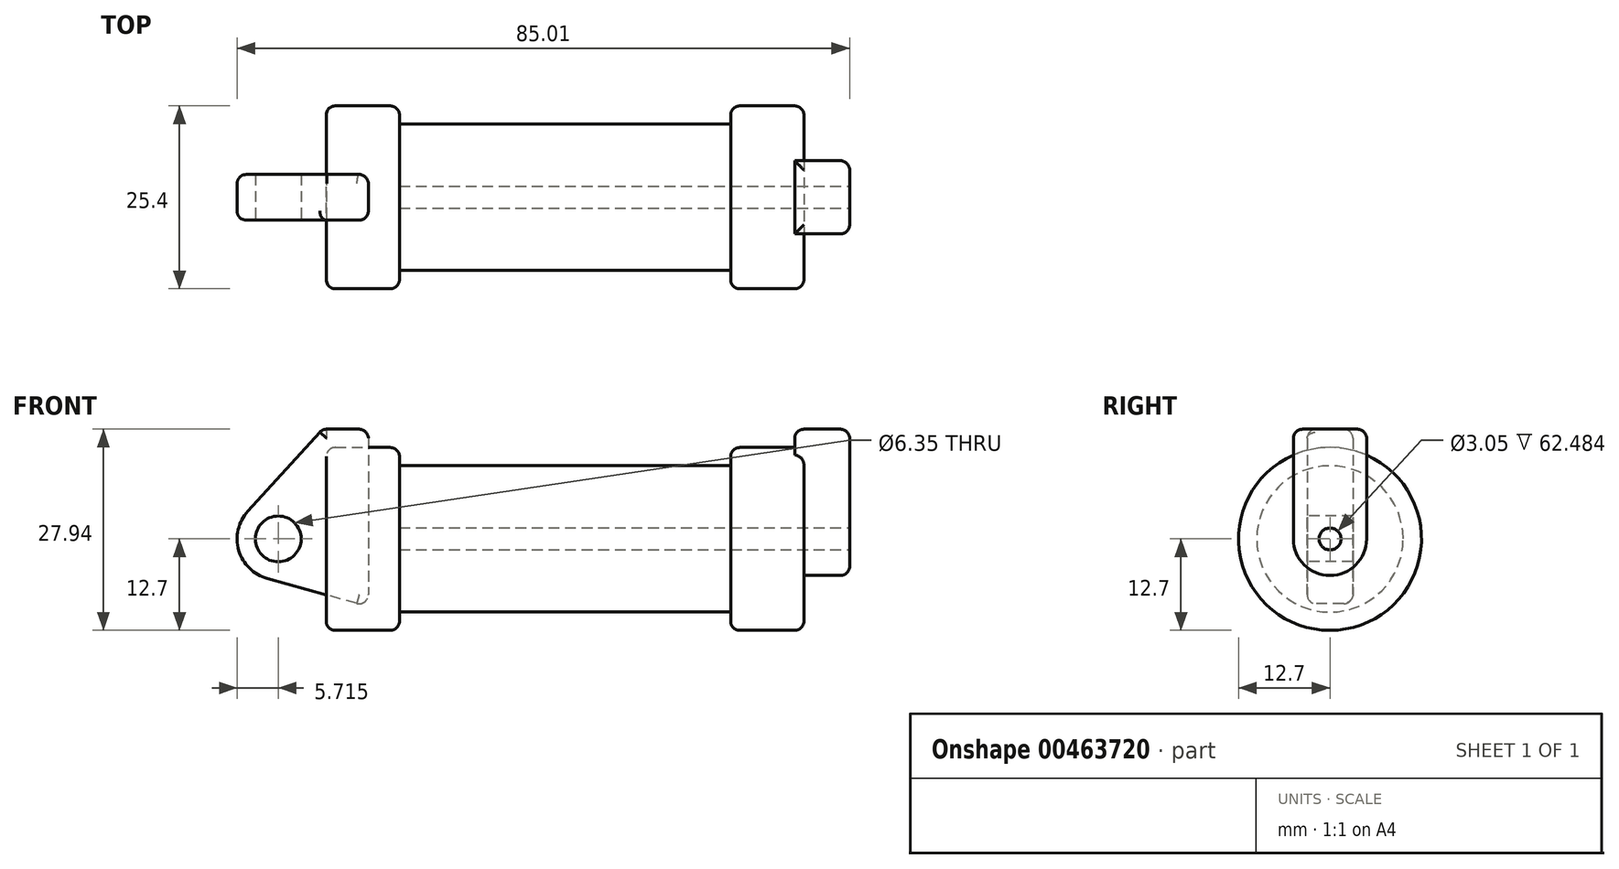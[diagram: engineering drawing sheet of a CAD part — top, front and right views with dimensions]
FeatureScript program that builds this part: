
annotation { "Feature Type Name" : "Feature", "Feature Type Description" : "" }
export const myFeature = defineFeature(function(context is Context, id is Id, definition is map)
    precondition{}
    {
        {
            var Q0;
            Q0=qCreatedBy(makeId("Front.planeOp"),FACE);
            var sketch = newSketch(context, id + "F0", { "sketchPlane" : qUnion([Q0])});
            skLineSegment(sketch, "E0", {"start": v(0, 0) * mm, "end": v(0, 12.7) * mm});
            skLineSegment(sketch, "E1", {"start": v(0, 12.7) * mm, "end": v(10.16, 12.7) * mm});
            skLineSegment(sketch, "E2", {"start": v(10.16, 12.7) * mm, "end": v(10.16, 10.16) * mm});
            skLineSegment(sketch, "E3", {"start": v(10.16, 10.16) * mm, "end": v(56.13, 10.16) * mm});
            skLineSegment(sketch, "E4", {"start": v(56.13, 10.16) * mm, "end": v(56.13, 12.7) * mm});
            skLineSegment(sketch, "E5", {"start": v(56.13, 12.7) * mm, "end": v(66.3, 12.7) * mm});
            skLineSegment(sketch, "E6", {"start": v(66.3, 12.7) * mm, "end": v(66.3, 0) * mm});
            skLineSegment(sketch, "E7", {"start": v(66.3, 0) * mm, "end": v(0, 0) * mm});
            skLineSegment(sketch, "E8", {"start": v(5.84, 15.24) * mm, "end": v(-0.5, 15.24) * mm});
            skLineSegment(sketch, "E9", {"start": v(-0.5, 15.24) * mm, "end": v(-10.88, 3.85) * mm});
            skLineSegment(sketch, "E10", {"start": v(0, 0) * mm, "end": v(-6.65, 0) * mm});
            skCircle(sketch, "E11", {"center": v(-6.65, 0) * mm, "radius": 5.72 * mm});
            skCircle(sketch, "E12", {"center": v(-6.65, 0) * mm, "radius": 3.18 * mm});
            skLineSegment(sketch, "E13", {"start": v(5.84, 15.24) * mm, "end": v(5.84, -9.4) * mm});
            skLineSegment(sketch, "E14", {"start": v(5.84, -9.4) * mm, "end": v(-8.18, -5.5) * mm});
            skSolve(sketch);
        }
        {
            var Q0;
            {var subQ0=sQuery(id+"F0.wireOp",EDGE,"E0");Q0=makeQuery(id+"F0.imprint","IMPRINT",FACE,{"disambiguationData":[TD([[makeQuery(id+"F0.imprint","IMPRINT",EDGE,{"derivedFrom":subQ0}),-1.0]])]});}
            var Q1;
            {var subQ1=sQuery(id+"F0.wireOp",EDGE,"E0");Q1=makeQuery(id+"F0.imprint","IMPRINT",FACE,{"disambiguationData":[TD([[makeQuery(id+"F0.imprint","IMPRINT",EDGE,{"derivedFrom":subQ1}),1.0]])]});}
            var Q2;
            {var subQ0=sQuery(id+"F0.wireOp",EDGE,"E14");Q2=makeQuery(id+"F0.imprint","IMPRINT",FACE,{"disambiguationData":[TD([[makeQuery(id+"F0.imprint","IMPRINT",EDGE,{"derivedFrom":subQ0}),-1.0]])]});}
            var Q3;
            {var subQ5=sQuery(id+"F0.wireOp",EDGE,"E12");Q3=makeQuery(id+"F0.imprint","IMPRINT",FACE,{"disambiguationData":[TD([[makeQuery(id+"F0.imprint","IMPRINT",EDGE,{"derivedFrom":subQ5}),-1.0]])]});}
            extrude(context, id + "F1", {"entities" : qUnion([Q0, Q1, Q2, Q3]), "endBound" : BoundingType.SYMMETRIC, "oppositeDirection" : true, "depth" : 6.35 * mm});
        }
        {
            var Q0;
            {var subQ0=sQuery(id+"F0.wireOp",EDGE,"E2");Q0=makeQuery(id+"F0.imprint","IMPRINT",FACE,{"disambiguationData":[TD([[makeQuery(id+"F0.imprint","IMPRINT",EDGE,{"derivedFrom":subQ0}),-1.0]])]});}
            var Q1;
            {var subQ0=sQuery(id+"F0.wireOp",EDGE,"E0");Q1=makeQuery(id+"F0.imprint","IMPRINT",FACE,{"disambiguationData":[TD([[makeQuery(id+"F0.imprint","IMPRINT",EDGE,{"derivedFrom":subQ0}),-1.0]])]});}
            var Q2;
            Q2=sQuery(id+"F0.wireOp",EDGE,"E7");
            revolve(context, id + "F2", {"entities" : qUnion([Q0, Q1]), "axis" : qUnion([Q2]), "revolveType" : RevolveType.FULL});
        }
        {
            var Q0;
            Q0=makeQuery(id+"F2.opRevolve","SWEPT_FACE",FACE,{"disambiguationData":[OSD([sQuery(id+"F0.wireOp",EDGE,"E6")])]});
            var sketch = newSketch(context, id + "F3", { "sketchPlane" : qUnion([Q0])});
            skCircle(sketch, "E15", {"center": v(0, 0) * mm, "radius": 1.52 * mm});
            skCircle(sketch, "E16", {"center": v(0, 0) * mm, "radius": 5.08 * mm});
            skLineSegment(sketch, "E17", {"start": v(5.08, 0) * mm, "end": v(5.08, 15.24) * mm});
            skLineSegment(sketch, "E18", {"start": v(-5.08, 0) * mm, "end": v(-5.08, 15.24) * mm});
            skLineSegment(sketch, "E19", {"start": v(-5.08, 15.24) * mm, "end": v(5.08, 15.24) * mm});
            skSolve(sketch);
        }
        {
            var Q0;
            Q0=makeQuery(id+"F3.imprint","IMPRINT",FACE,{"disambiguationData":[TD([[makeQuery(id+"F3.imprint","IMPRINT",EDGE,{"derivedFrom":sQuery(id+"F3.wireOp",EDGE,"E15")}),1.0]])]});
            var Q1;
            Q1=makeQuery(id+"F2.opRevolve","SWEPT_FACE",FACE,{"disambiguationData":[OSD([sQuery(id+"F0.wireOp",EDGE,"E2")])]});
            extrude(context, id + "F4", {"entities" : qUnion([Q0]), "operationType" : NewBodyOperationType.REMOVE, "endBound" : BoundingType.UP_TO_SURFACE, "oppositeDirection" : true, "endBoundEntityFace" : qUnion([Q1]), "depth" : 25.4 * mm});
        }
        {
            var Q0;
            {var subQ0=sQuery(id+"F3.wireOp",EDGE,"E19");Q0=makeQuery(id+"F3.imprint","IMPRINT",FACE,{"disambiguationData":[TD([[makeQuery(id+"F3.imprint","IMPRINT",EDGE,{"derivedFrom":subQ0}),-1.0]])]});}
            extrude(context, id + "F5", {"entities" : qUnion([Q0]), "operationType" : NewBodyOperationType.ADD, "oppositeDirection" : true, "depth" : 1.27 * mm});
        }
        {
            var Q0;
            Q0 = qSketchRegion(id + "F3", true);
            extrude(context, id + "F6", {"entities" : qUnion([Q0]), "operationType" : NewBodyOperationType.ADD, "depth" : 6.35 * mm});
        }
        {
            var Q0;
            Q0=makeQuery(id+"F2.opRevolve","SWEPT_EDGE",EDGE,{"disambiguationData":[OSD([sQuery(id+"F0.wireOp",EDGE,"E0"),sQuery(id+"F0.wireOp",EDGE,"E1")])]});
            var Q1;
            Q1=makeQuery(id+"F2.opRevolve","SWEPT_EDGE",EDGE,{"disambiguationData":[OSD([sQuery(id+"F0.wireOp",EDGE,"E1"),sQuery(id+"F0.wireOp",EDGE,"E2")])]});
            var Q2;
            Q2=makeQuery(id+"F1.opExtrude","CAP_EDGE",EDGE,{"disambiguationData":[OSD([sQuery(id+"F0.wireOp",EDGE,"E14")])],"isStart":true});
            fillet(context, id + "F7", {"entities" : qUnion([Q0, Q1, Q2]), "radius" : 1.27 * mm, "tangentPropagation" : true, "allowEdgeOverflow" : false});
        }
        {
            var Q0;
            Q0=makeQuery(id+"F2.opRevolve","SWEPT_EDGE",EDGE,{"disambiguationData":[OSD([sQuery(id+"F0.wireOp",EDGE,"E4"),sQuery(id+"F0.wireOp",EDGE,"E5")])]});
            var Q1;
            Q1=makeQuery(id+"F2.opRevolve","SWEPT_EDGE",EDGE,{"disambiguationData":[OSD([sQuery(id+"F0.wireOp",EDGE,"E5"),sQuery(id+"F0.wireOp",EDGE,"E6")])]});
            fillet(context, id + "F8", {"entities" : qUnion([Q0, Q1]), "radius" : 1.27 * mm, "tangentPropagation" : true, "allowEdgeOverflow" : false});
        }
        {
            var Q0;
            Q0=makeQuery(id+"F1.opExtrude","SWEPT_EDGE",EDGE,{"disambiguationData":[OSD([sQuery(id+"F0.wireOp",EDGE,"E8"),sQuery(id+"F0.wireOp",EDGE,"E13")])]});
            var Q1;
            Q1=makeQuery(id+"F1.opExtrude","CAP_EDGE",EDGE,{"disambiguationData":[OSD([sQuery(id+"F0.wireOp",EDGE,"E8")])],"isStart":false});
            fillet(context, id + "F9", {"entities" : qUnion([Q0, Q1]), "radius" : 1.27 * mm, "tangentPropagation" : true, "allowEdgeOverflow" : false});
        }
        {
            var Q0;
            Q0=makeQuery(id+"F1.opExtrude","CAP_EDGE",EDGE,{"disambiguationData":[OSD([sQuery(id+"F0.wireOp",EDGE,"E8")])],"isStart":true});
            fillet(context, id + "F10", {"entities" : qUnion([Q0]), "radius" : 1.27 * mm, "tangentPropagation" : true, "allowEdgeOverflow" : false});
        }
        {
            var Q0;
            Q0=makeQuery(id+"F6.opExtrude","CAP_EDGE",EDGE,{"disambiguationData":[OSD([sQuery(id+"F3.wireOp",EDGE,"E19")])],"isStart":false});
            var Q1;
            {var subQ0=sQuery(id+"F3.wireOp",EDGE,"E19");var subQ1=sQuery(id+"F3.wireOp",EDGE,"E18");Q1=makeQuery(id+"F6.boolean.opBoolean","MERGE",EDGE,{"derivedFrom":[makeQuery(id+"F5.opExtrude","SWEPT_EDGE",EDGE,{"disambiguationData":[OSD([subQ1,subQ0])]}),makeQuery(id+"F6.opExtrude","SWEPT_EDGE",EDGE,{"disambiguationData":[OSD([subQ1,subQ0])]})]});}
            var Q2;
            {var subQ0=sQuery(id+"F3.wireOp",EDGE,"E19");var subQ1=sQuery(id+"F3.wireOp",EDGE,"E17");Q2=makeQuery(id+"F6.boolean.opBoolean","MERGE",EDGE,{"derivedFrom":[makeQuery(id+"F5.opExtrude","SWEPT_EDGE",EDGE,{"disambiguationData":[OSD([subQ1,subQ0])]}),makeQuery(id+"F6.opExtrude","SWEPT_EDGE",EDGE,{"disambiguationData":[OSD([subQ1,subQ0])]})]});}
            var Q3;
            Q3=makeQuery(id+"F5.opExtrude","CAP_EDGE",EDGE,{"disambiguationData":[OSD([sQuery(id+"F3.wireOp",EDGE,"E19")])],"isStart":false});
            var Q4;
            Q4=makeQuery(id+"F6.opExtrude","CAP_EDGE",EDGE,{"disambiguationData":[OSD([sQuery(id+"F3.wireOp",EDGE,"E18")])],"isStart":false});
            var Q5;
            Q5=makeQuery(id+"F1.opExtrude","CAP_EDGE",EDGE,{"disambiguationData":[OSD([sQuery(id+"F0.wireOp",EDGE,"E13")])],"isStart":false});
            fillet(context, id + "F11", {"entities" : qUnion([Q0, Q1, Q2, Q3, Q4, Q5]), "radius" : 1.27 * mm, "tangentPropagation" : true, "allowEdgeOverflow" : false});
        }
    });
